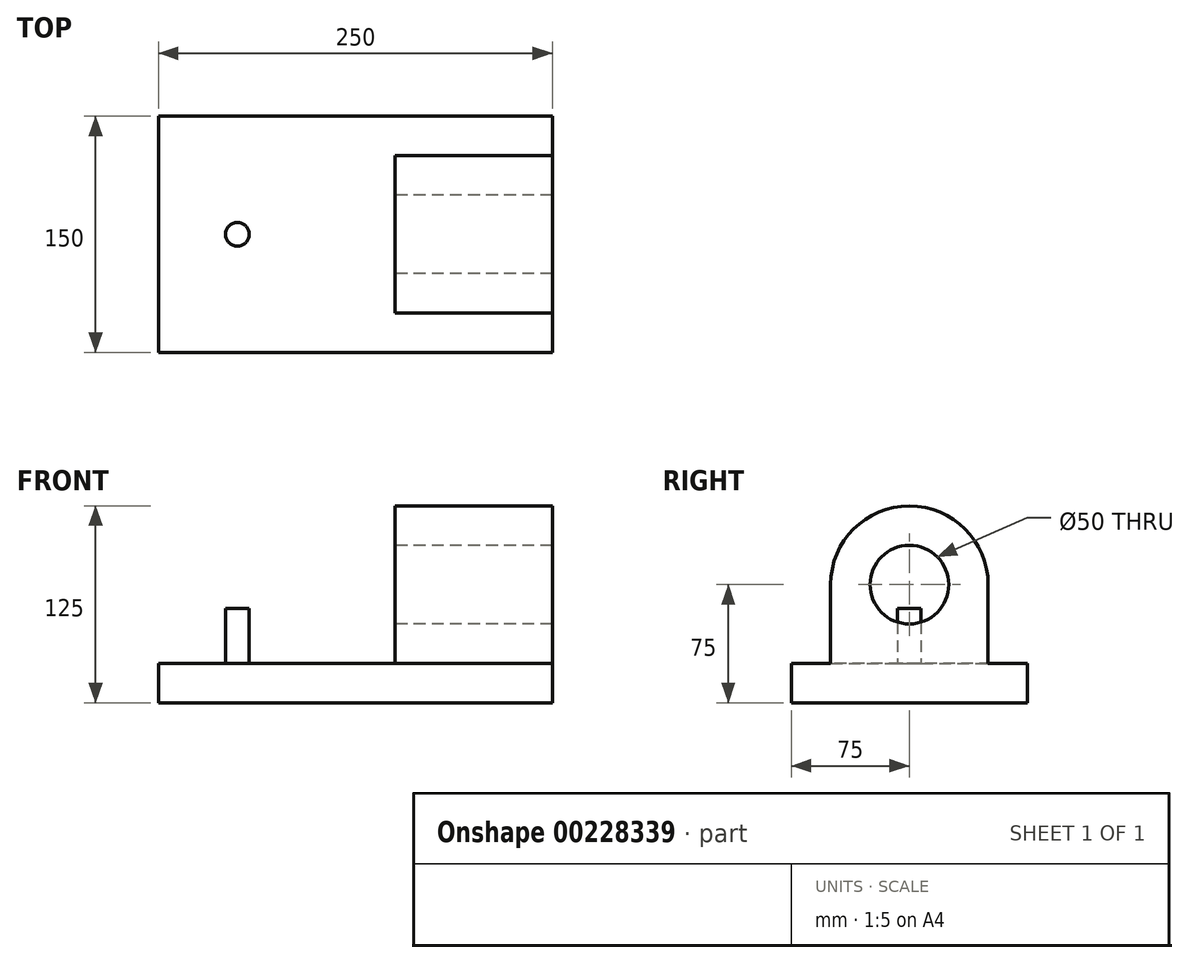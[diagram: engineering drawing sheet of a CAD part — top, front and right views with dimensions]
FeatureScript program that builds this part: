
annotation { "Feature Type Name" : "Feature", "Feature Type Description" : "" }
export const myFeature = defineFeature(function(context is Context, id is Id, definition is map)
    precondition{}
    {
        {
            var Q0;
            Q0=qCreatedBy(makeId("Top.planeOp"),FACE);
            var sketch = newSketch(context, id + "F0", { "sketchPlane" : qUnion([Q0])});
            skLineSegment(sketch, "E0.bottom", {"start": v(125, 75) * mm, "end": v(-125, 75) * mm});
            skLineSegment(sketch, "E0.top", {"start": v(125, -75) * mm, "end": v(-125, -75) * mm});
            skLineSegment(sketch, "E0.left", {"start": v(125, 75) * mm, "end": v(125, -75) * mm});
            skLineSegment(sketch, "E0.right", {"start": v(-125, 75) * mm, "end": v(-125, -75) * mm});
            skPoint(sketch, "E0.middle", {"position": v(0, 0) * mm});
            skSolve(sketch);
        }
        {
            var Q0;
            Q0=makeQuery(id+"F0.imprint","IMPRINT",FACE,{"disambiguationData":[TD([[makeQuery(id+"F0.imprint","IMPRINT",EDGE,{"derivedFrom":sQuery(id+"F0.wireOp",EDGE,"E0.bottom")}),1.0]])]});
            extrude(context, id + "F7", {"entities" : qUnion([Q0]), "depth" : 25 * mm});
        }
        {
            var Q0;
            Q0=makeQuery(id+"F7.opExtrude","CAP_FACE",FACE,{"disambiguationData":[OSD([sQuery(id+"F0.wireOp",EDGE,"E0.bottom"),sQuery(id+"F0.wireOp",EDGE,"E0.top"),sQuery(id+"F0.wireOp",EDGE,"E0.left"),sQuery(id+"F0.wireOp",EDGE,"E0.right")])],"isStart":false});
            var sketch = newSketch(context, id + "F1", { "sketchPlane" : qUnion([Q0])});
            skCircle(sketch, "E1", {"center": v(-75, 0) * mm, "radius": 7.5 * mm});
            skSolve(sketch);
        }
        {
            var Q0;
            Q0=makeQuery(id+"F1.imprint","IMPRINT",FACE,{"disambiguationData":[TD([[makeQuery(id+"F1.imprint","IMPRINT",EDGE,{"derivedFrom":sQuery(id+"F1.wireOp",EDGE,"E1")}),1.0]])]});
            extrude(context, id + "F2", {"entities" : qUnion([Q0]), "operationType" : NewBodyOperationType.ADD, "depth" : 35 * mm});
        }
        {
            var Q0;
            Q0=makeQuery(id+"F7.opExtrude","CAP_FACE",FACE,{"disambiguationData":[OSD([sQuery(id+"F0.wireOp",EDGE,"E0.bottom"),sQuery(id+"F0.wireOp",EDGE,"E0.top"),sQuery(id+"F0.wireOp",EDGE,"E0.left"),sQuery(id+"F0.wireOp",EDGE,"E0.right")])],"isStart":false});
            var sketch = newSketch(context, id + "F3", { "sketchPlane" : qUnion([Q0])});
            skLineSegment(sketch, "E2.bottom", {"start": v(125, -50) * mm, "end": v(25, -50) * mm});
            skLineSegment(sketch, "E2.top", {"start": v(125, 50) * mm, "end": v(25, 50) * mm});
            skLineSegment(sketch, "E2.left", {"start": v(125, -50) * mm, "end": v(125, 50) * mm});
            skLineSegment(sketch, "E3", {"start": v(25, -50) * mm, "end": v(25, 50) * mm});
            skSolve(sketch);
        }
        {
            var Q0;
            Q0=makeQuery(id+"F3.imprint","IMPRINT",FACE,{"disambiguationData":[TD([[makeQuery(id+"F3.imprint","IMPRINT",EDGE,{"derivedFrom":sQuery(id+"F3.wireOp",EDGE,"E2.bottom")}),-1.0]])]});
            extrude(context, id + "F4", {"entities" : qUnion([Q0]), "operationType" : NewBodyOperationType.ADD, "depth" : 100 * mm});
        }
        {
            var Q0;
            Q0=makeQuery(id+"F4.opExtrude","SWEPT_FACE",FACE,{"disambiguationData":[OSD([sQuery(id+"F3.wireOp",EDGE,"E3")])]});
            var sketch = newSketch(context, id + "F5", { "sketchPlane" : qUnion([Q0])});
            skCircle(sketch, "E4", {"center": v(0, 75) * mm, "radius": 25 * mm});
            skPoint(sketch, "E4.centerSnap0", {"position": v(-50, 75) * mm});
            skSolve(sketch);
        }
        {
            var Q0;
            Q0=makeQuery(id+"F5.imprint","IMPRINT",FACE,{"disambiguationData":[TD([[makeQuery(id+"F5.imprint","IMPRINT",EDGE,{"derivedFrom":sQuery(id+"F5.wireOp",EDGE,"E4")}),1.0]])]});
            extrude(context, id + "F8", {"entities" : qUnion([Q0]), "operationType" : NewBodyOperationType.REMOVE, "endBound" : BoundingType.THROUGH_ALL, "oppositeDirection" : true, "depth" : 25 * mm});
        }
        {
            var Q0;
            Q0=makeQuery(id+"F4.opExtrude","CAP_EDGE",EDGE,{"disambiguationData":[OSD([sQuery(id+"F3.wireOp",EDGE,"E2.top")])],"isStart":false});
            var Q1;
            Q1=makeQuery(id+"F4.opExtrude","CAP_EDGE",EDGE,{"disambiguationData":[OSD([sQuery(id+"F3.wireOp",EDGE,"E2.bottom")])],"isStart":false});
            fillet(context, id + "F6", {"entities" : qUnion([Q0, Q1]), "radius" : 50 * mm, "tangentPropagation" : true, "allowEdgeOverflow" : false});
        }
    });
